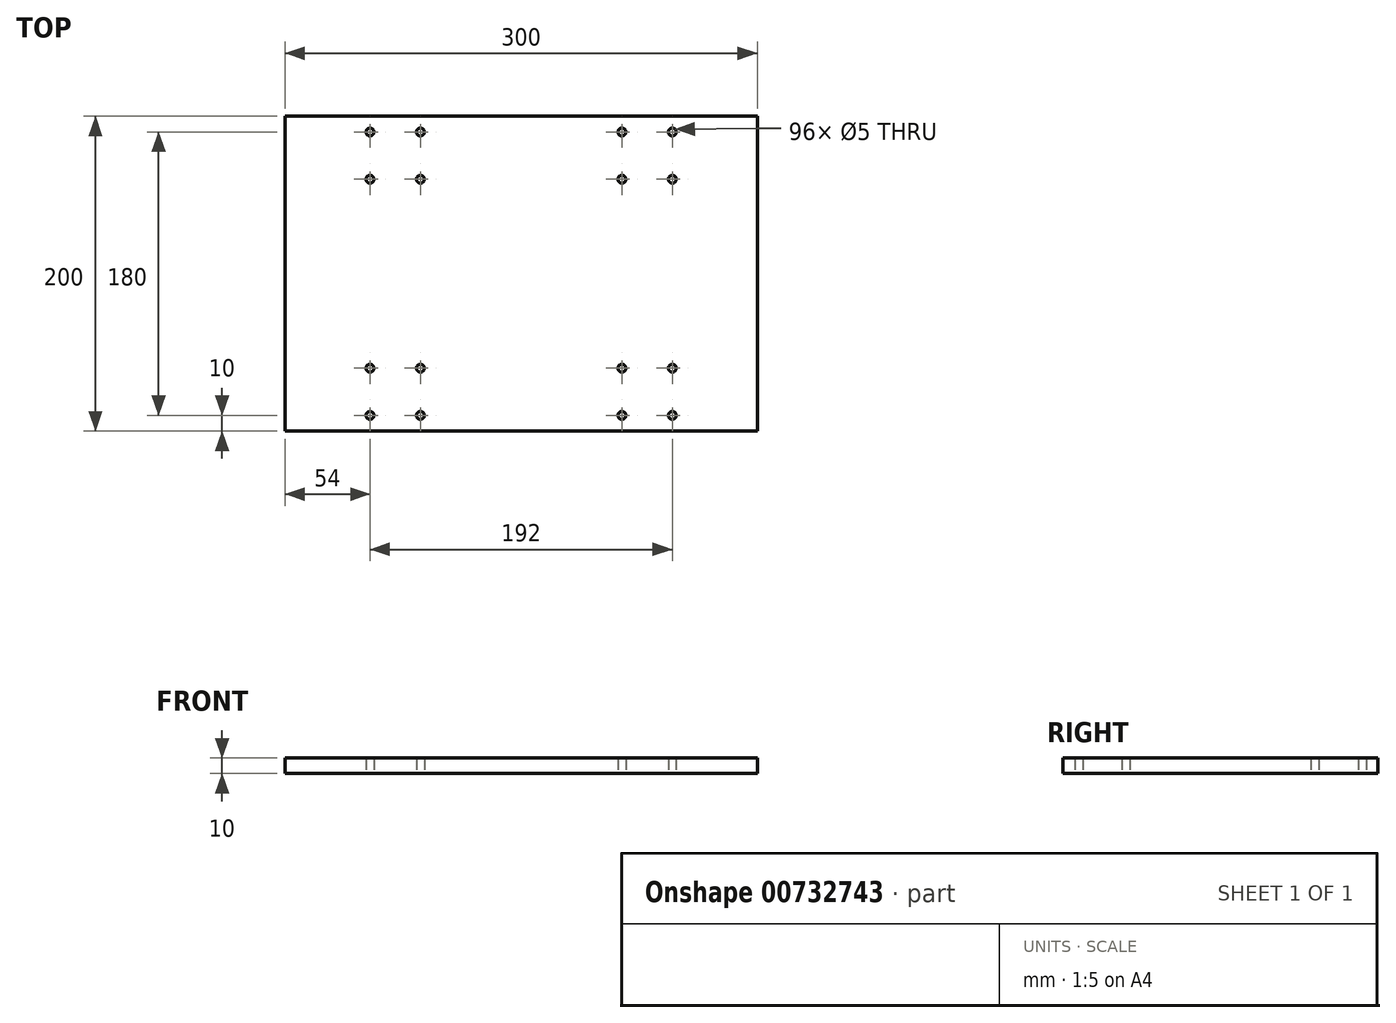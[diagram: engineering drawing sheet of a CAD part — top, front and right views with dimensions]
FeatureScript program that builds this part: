
annotation { "Feature Type Name" : "Feature", "Feature Type Description" : "" }
export const myFeature = defineFeature(function(context is Context, id is Id, definition is map)
    precondition{}
    {
        {
            var Q0;
            Q0=qCreatedBy(makeId("Top.planeOp"),FACE);
            var sketch = newSketch(context, id + "F0", { "sketchPlane" : qUnion([Q0])});
            skLineSegment(sketch, "E0.bottom", {"start": v(150, -100) * mm, "end": v(-150, -100) * mm});
            skLineSegment(sketch, "E0.top", {"start": v(150, 100) * mm, "end": v(-150, 100) * mm});
            skLineSegment(sketch, "E0.left", {"start": v(150, -100) * mm, "end": v(150, 100) * mm});
            skLineSegment(sketch, "E0.right", {"start": v(-150, -100) * mm, "end": v(-150, 100) * mm});
            skPoint(sketch, "E0.middle", {"position": v(0, 0) * mm});
            skLineSegment(sketch, "E1", {"start": v(-80, 100) * mm, "end": v(-80, -100) * mm, "construction": true});
            skLineSegment(sketch, "E2.bottom", {"start": v(-64, -90) * mm, "end": v(-96, -90) * mm, "construction": true});
            skLineSegment(sketch, "E2.top", {"start": v(-64, -60) * mm, "end": v(-96, -60) * mm, "construction": true});
            skLineSegment(sketch, "E2.left", {"start": v(-64, -90) * mm, "end": v(-64, -60) * mm, "construction": true});
            skLineSegment(sketch, "E2.right", {"start": v(-96, -90) * mm, "end": v(-96, -60) * mm, "construction": true});
            skPoint(sketch, "E2.middle", {"position": v(-80, -75) * mm});
            skCircle(sketch, "E3", {"center": v(-96, -90) * mm, "radius": 2.5 * mm});
            skCircle(sketch, "E4", {"center": v(-96, -60) * mm, "radius": 2.5 * mm});
            skCircle(sketch, "E5", {"center": v(-64, -60) * mm, "radius": 2.5 * mm});
            skCircle(sketch, "E6", {"center": v(-64, -90) * mm, "radius": 2.5 * mm});
            skCircle(sketch, "E7.MirrorC", {"center": v(-64, 60) * mm, "radius": 2.5 * mm});
            skCircle(sketch, "E8.MirrorC", {"center": v(-96, 60) * mm, "radius": 2.5 * mm});
            skCircle(sketch, "E9.MirrorC", {"center": v(-96, 90) * mm, "radius": 2.5 * mm});
            skCircle(sketch, "E10.MirrorC", {"center": v(-64, 90) * mm, "radius": 2.5 * mm});
            skLineSegment(sketch, "E11.MirrorCS", {"start": v(80, 100) * mm, "end": v(80, -100) * mm, "construction": true});
            skCircle(sketch, "E12.MirrorC", {"center": v(64, -90) * mm, "radius": 2.5 * mm});
            skCircle(sketch, "E13.MirrorC", {"center": v(64, -60) * mm, "radius": 2.5 * mm});
            skCircle(sketch, "E14.MirrorC", {"center": v(96, -60) * mm, "radius": 2.5 * mm});
            skCircle(sketch, "E15.MirrorC", {"center": v(96, -90) * mm, "radius": 2.5 * mm});
            skCircle(sketch, "E16.MirrorC", {"center": v(64, 60) * mm, "radius": 2.5 * mm});
            skCircle(sketch, "E17.MirrorC", {"center": v(96, 60) * mm, "radius": 2.5 * mm});
            skCircle(sketch, "E18.MirrorC", {"center": v(96, 90) * mm, "radius": 2.5 * mm});
            skCircle(sketch, "E19.MirrorC", {"center": v(64, 90) * mm, "radius": 2.5 * mm});
            skSolve(sketch);
        }
        {
            var Q0;
            Q0 = qSketchRegion(id + "F0", true);
            extrude(context, id + "F1", {"entities" : qUnion([Q0]), "depth" : 10 * mm, "offsetDistance" : 25 * mm});
        }
    });
